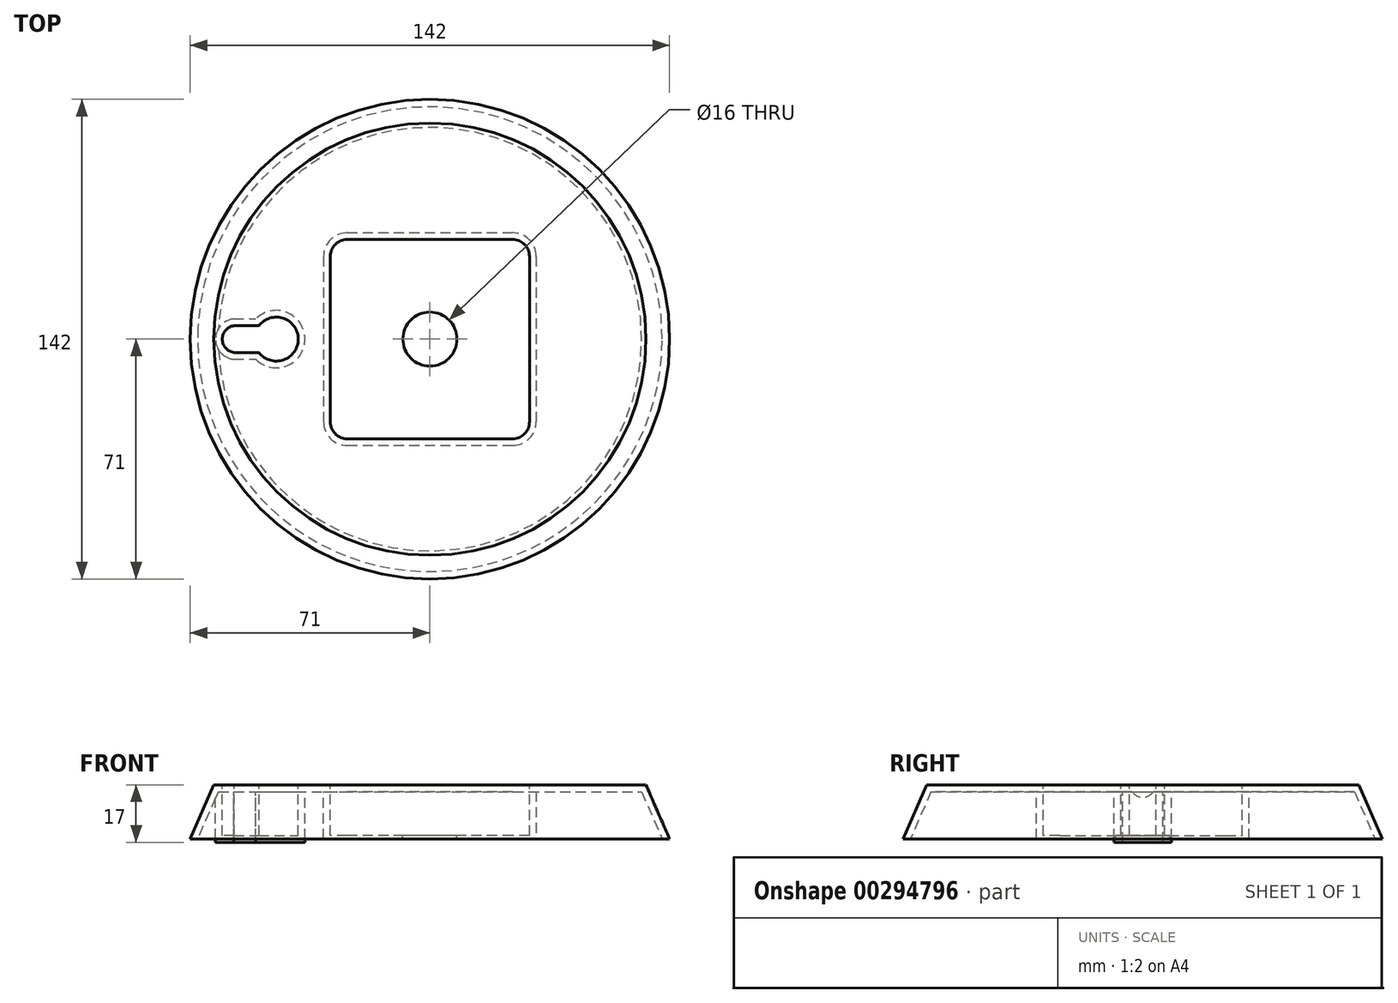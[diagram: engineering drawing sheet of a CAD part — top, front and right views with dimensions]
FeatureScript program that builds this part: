
annotation { "Feature Type Name" : "Feature", "Feature Type Description" : "" }
export const myFeature = defineFeature(function(context is Context, id is Id, definition is map)
    precondition{}
    {
        {
            var Q0;
            Q0=qCreatedBy(makeId("Top.planeOp"),FACE);
            var sketch = newSketch(context, id + "F0", { "sketchPlane" : qUnion([Q0])});
            skCircle(sketch, "E0", {"center": v(0, 0) * mm, "radius": 71 * mm});
            skSolve(sketch);
        }
        {
            var Q0;
            Q0=qCreatedBy(makeId("Top.planeOp"),FACE);
            cPlane(context, id + "F1", {"entities" : qUnion([Q0]), "cplaneType" : CPlaneType.OFFSET, "offset" : 16 * mm, "width" : 150 * mm, "height" : 150 * mm});
        }
        {
            var Q0;
            Q0=qCreatedBy(id+"F1.planeOp",FACE);
            var sketch = newSketch(context, id + "F2", { "sketchPlane" : qUnion([Q0])});
            skCircle(sketch, "E1", {"center": v(0, 0) * mm, "radius": 64 * mm});
            skSolve(sketch);
        }
        {
            var Q0;
            Q0=makeQuery(id+"F2.imprint","IMPRINT",FACE,{"disambiguationData":[TD([[makeQuery(id+"F2.imprint","IMPRINT",EDGE,{"derivedFrom":sQuery(id+"F2.wireOp",EDGE,"E1")}),1.0]])]});
            var Q1;
            Q1=makeQuery(id+"F0.imprint","IMPRINT",FACE,{"disambiguationData":[TD([[makeQuery(id+"F0.imprint","IMPRINT",EDGE,{"derivedFrom":sQuery(id+"F0.wireOp",EDGE,"E0")}),1.0]])]});
            loft(context, id + "F3", {"sheetProfilesArray" : [{ "sheetProfileEntities" : qUnion([Q0]) }, { "sheetProfileEntities" : qUnion([Q1]) }]});
        }
        {
            var Q0;
            Q0=makeQuery(id+"F3.opLoft","CAP_FACE",FACE,{"disambiguationData":[OSD([makeQuery(id+"F2.imprint","IMPRINT",FACE,{"disambiguationData":[TD([[makeQuery(id+"F2.imprint","IMPRINT",EDGE,{"derivedFrom":sQuery(id+"F2.wireOp",EDGE,"E1")}),1.0]])]})])],"isStart":true});
            var sketch = newSketch(context, id + "F4", { "sketchPlane" : qUnion([Q0])});
            skLineSegment(sketch, "E2.bottom", {"start": v(24.5, -29.5) * mm, "end": v(-24.5, -29.5) * mm});
            skLineSegment(sketch, "E2.top", {"start": v(24.5, 29.5) * mm, "end": v(-24.5, 29.5) * mm});
            skLineSegment(sketch, "E2.left", {"start": v(29.5, -24.5) * mm, "end": v(29.5, 24.5) * mm});
            skLineSegment(sketch, "E2.right", {"start": v(-29.5, -24.5) * mm, "end": v(-29.5, 24.5) * mm});
            skPoint(sketch, "E2.middle", {"position": v(0, 0) * mm});
            skArc(sketch, "E3", {"start": v(-50.65, -3.97) * mm, "mid": v(-39, 0) * mm, "end": v(-50.65, 3.97) * mm});
            skArc(sketch, "E4", {"start": v(-58, 3.97) * mm, "mid": v(-61.5, 0) * mm, "end": v(-58, -3.97) * mm});
            skLineSegment(sketch, "E5", {"start": v(-58, -3.97) * mm, "end": v(-50.65, -3.97) * mm});
            skLineSegment(sketch, "E6", {"start": v(-58, 3.97) * mm, "end": v(-50.65, 3.97) * mm});
            skPoint(sketch, "E7.visualSharp", {"position": v(-29.5, 29.5) * mm});
            skArc(sketch, "E7.filletArc", {"start": v(-24.5, 29.5) * mm, "mid": v(-28.04, 28.04) * mm, "end": v(-29.5, 24.5) * mm});
            skPoint(sketch, "E8.visualSharp", {"position": v(29.5, 29.5) * mm});
            skArc(sketch, "E8.filletArc", {"start": v(29.5, 24.5) * mm, "mid": v(28.04, 28.04) * mm, "end": v(24.5, 29.5) * mm});
            skPoint(sketch, "E9.visualSharp", {"position": v(29.5, -29.5) * mm});
            skArc(sketch, "E9.filletArc", {"start": v(24.5, -29.5) * mm, "mid": v(28.04, -28.04) * mm, "end": v(29.5, -24.5) * mm});
            skPoint(sketch, "E10.visualSharp", {"position": v(-29.5, -29.5) * mm});
            skArc(sketch, "E10.filletArc", {"start": v(-29.5, -24.5) * mm, "mid": v(-28.04, -28.04) * mm, "end": v(-24.5, -29.5) * mm});
            skSolve(sketch);
        }
        {
            var Q0;
            Q0=makeQuery(id+"F4.imprint","IMPRINT",FACE,{"disambiguationData":[TD([[makeQuery(id+"F4.imprint","IMPRINT",EDGE,{"derivedFrom":sQuery(id+"F4.wireOp",EDGE,"E2.bottom")}),-1.0]])]});
            var Q1;
            Q1=makeQuery(id+"F4.imprint","IMPRINT",FACE,{"disambiguationData":[TD([[makeQuery(id+"F4.imprint","IMPRINT",EDGE,{"derivedFrom":sQuery(id+"F4.wireOp",EDGE,"E3")}),1.0]])]});
            extrude(context, id + "F5", {"entities" : qUnion([Q0, Q1]), "operationType" : NewBodyOperationType.REMOVE, "oppositeDirection" : true, "depth" : 15 * mm});
        }
        {
            var Q0;
            Q0=makeQuery(id+"F5.boolean.opBoolean","COPY",FACE,{"derivedFrom":makeQuery(id+"F5.opExtrude","CAP_FACE",FACE,{"disambiguationData":[OSD([sQuery(id+"F4.wireOp",EDGE,"E2.bottom"),sQuery(id+"F4.wireOp",EDGE,"E2.top"),sQuery(id+"F4.wireOp",EDGE,"E2.left"),sQuery(id+"F4.wireOp",EDGE,"E2.right"),sQuery(id+"F4.wireOp",EDGE,"E7.filletArc"),sQuery(id+"F4.wireOp",EDGE,"E8.filletArc"),sQuery(id+"F4.wireOp",EDGE,"E9.filletArc"),sQuery(id+"F4.wireOp",EDGE,"E10.filletArc")])],"isStart":false})});
            var sketch = newSketch(context, id + "F6", { "sketchPlane" : qUnion([Q0])});
            skCircle(sketch, "E11", {"center": v(0, 0) * mm, "radius": 8 * mm});
            skSolve(sketch);
        }
        {
            var Q0;
            Q0 = qSketchRegion(id + "F6", true);
            extrude(context, id + "F7", {"entities" : qUnion([Q0]), "operationType" : NewBodyOperationType.REMOVE, "endBound" : BoundingType.THROUGH_ALL, "oppositeDirection" : true, "depth" : 25 * mm});
        }
        {
            var Q0;
            Q0=makeQuery(id+"F3.opLoft","CAP_FACE",FACE,{"disambiguationData":[OSD([makeQuery(id+"F0.imprint","IMPRINT",FACE,{"disambiguationData":[TD([[makeQuery(id+"F0.imprint","IMPRINT",EDGE,{"derivedFrom":sQuery(id+"F0.wireOp",EDGE,"E0")}),1.0]])]})])],"isStart":true});
            shell(context, id + "F8", {"entities" : qUnion([Q0]), "thickness" : 2 * mm});
        }
    });
